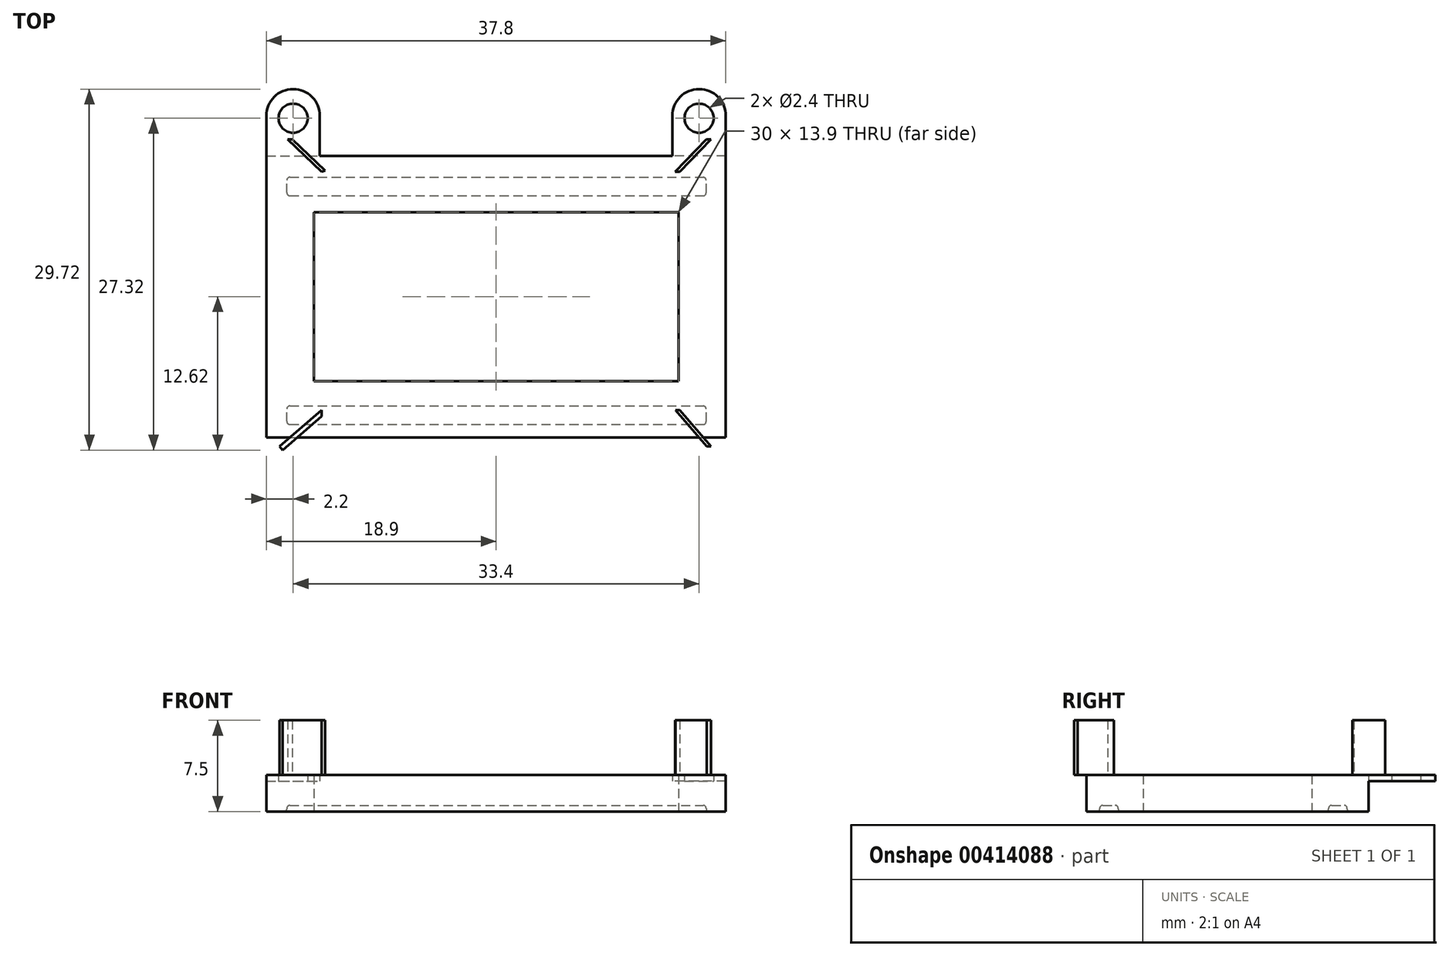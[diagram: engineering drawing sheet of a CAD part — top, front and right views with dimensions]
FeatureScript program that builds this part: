
annotation { "Feature Type Name" : "Feature", "Feature Type Description" : "" }
export const myFeature = defineFeature(function(context is Context, id is Id, definition is map)
    precondition{}
    {
        {
            var Q0;
            Q0=qCreatedBy(makeId("Top.planeOp"),FACE);
            var sketch = newSketch(context, id + "F0", { "sketchPlane" : qUnion([Q0])});
            skLineSegment(sketch, "E0.bottom", {"start": v(0, 0) * mm, "end": v(37.8, 0) * mm});
            skLineSegment(sketch, "E0.top", {"start": v(0, 23.2) * mm, "end": v(37.8, 23.2) * mm});
            skLineSegment(sketch, "E0.left", {"start": v(0, 0) * mm, "end": v(0, 23.2) * mm});
            skLineSegment(sketch, "E0.right", {"start": v(37.8, 0) * mm, "end": v(37.8, 23.2) * mm});
            skSolve(sketch);
        }
        {
            var Q0;
            Q0=makeQuery(id+"F0.imprint","IMPRINT",FACE,{"disambiguationData":[TD([[makeQuery(id+"F0.imprint","IMPRINT",EDGE,{"derivedFrom":sQuery(id+"F0.wireOp",EDGE,"E0.bottom")}),1.0]])]});
            extrude(context, id + "F1", {"entities" : qUnion([Q0]), "depth" : 3 * mm});
        }
        {
            var Q0;
            Q0=makeQuery(id+"F1.opExtrude","CAP_FACE",FACE,{"disambiguationData":[OSD([sQuery(id+"F0.wireOp",EDGE,"E0.bottom"),sQuery(id+"F0.wireOp",EDGE,"E0.top"),sQuery(id+"F0.wireOp",EDGE,"E0.left"),sQuery(id+"F0.wireOp",EDGE,"E0.right")])],"isStart":false});
            var sketch = newSketch(context, id + "F2", { "sketchPlane" : qUnion([Q0])});
            skLineSegment(sketch, "E1", {"start": v(4.54, 2.26) * mm, "end": v(1.07, -0.72) * mm});
            skLineSegment(sketch, "E2", {"start": v(1.07, -0.72) * mm, "end": v(1.32, -1.02) * mm});
            skLineSegment(sketch, "E3", {"start": v(1.32, -1.02) * mm, "end": v(4.54, 1.75) * mm});
            skLineSegment(sketch, "E4", {"start": v(4.54, 1.75) * mm, "end": v(4.54, 2.26) * mm});
            skLineSegment(sketch, "E5", {"start": v(34, 2.26) * mm, "end": v(36.57, -0.72) * mm});
            skLineSegment(sketch, "E6", {"start": v(36.57, -0.72) * mm, "end": v(36.23, -0.72) * mm});
            skLineSegment(sketch, "E7", {"start": v(36.23, -0.72) * mm, "end": v(33.66, 2.26) * mm});
            skLineSegment(sketch, "E8", {"start": v(33.66, 2.26) * mm, "end": v(34, 2.26) * mm});
            skLineSegment(sketch, "E9", {"start": v(34, 21.88) * mm, "end": v(36.57, 24.56) * mm});
            skLineSegment(sketch, "E10", {"start": v(36.57, 24.56) * mm, "end": v(36.21, 24.56) * mm});
            skLineSegment(sketch, "E11", {"start": v(36.21, 24.56) * mm, "end": v(33.64, 21.88) * mm});
            skLineSegment(sketch, "E12", {"start": v(33.64, 21.88) * mm, "end": v(34, 21.88) * mm});
            skLineSegment(sketch, "E13", {"start": v(4.54, 21.88) * mm, "end": v(1.75, 24.56) * mm});
            skLineSegment(sketch, "E14", {"start": v(1.75, 24.56) * mm, "end": v(2.13, 24.56) * mm});
            skLineSegment(sketch, "E15", {"start": v(2.13, 24.56) * mm, "end": v(4.82, 21.98) * mm});
            skLineSegment(sketch, "E16", {"start": v(4.82, 21.98) * mm, "end": v(4.54, 21.88) * mm});
            skSolve(sketch);
        }
        {
            var Q0;
            {var subQ0=sQuery(id+"F2.wireOp",EDGE,"E14");Q0=makeQuery(id+"F2.imprint","IMPRINT",FACE,{"disambiguationData":[TD([[makeQuery(id+"F2.imprint","IMPRINT",EDGE,{"derivedFrom":subQ0}),-1.0]])]});}
            var Q1;
            {var subQ0=sQuery(id+"F2.wireOp",EDGE,"E16");Q1=makeQuery(id+"F2.imprint","IMPRINT",FACE,{"disambiguationData":[TD([[makeQuery(id+"F2.imprint","IMPRINT",EDGE,{"derivedFrom":subQ0}),-1.0]])]});}
            var Q2;
            {var subQ0=sQuery(id+"F2.wireOp",EDGE,"E2");Q2=makeQuery(id+"F2.imprint","IMPRINT",FACE,{"disambiguationData":[TD([[makeQuery(id+"F2.imprint","IMPRINT",EDGE,{"derivedFrom":subQ0}),1.0]])]});}
            var Q3;
            {var subQ0=sQuery(id+"F2.wireOp",EDGE,"E4");Q3=makeQuery(id+"F2.imprint","IMPRINT",FACE,{"disambiguationData":[TD([[makeQuery(id+"F2.imprint","IMPRINT",EDGE,{"derivedFrom":subQ0}),1.0]])]});}
            var Q4;
            {var subQ0=sQuery(id+"F2.wireOp",EDGE,"E8");Q4=makeQuery(id+"F2.imprint","IMPRINT",FACE,{"disambiguationData":[TD([[makeQuery(id+"F2.imprint","IMPRINT",EDGE,{"derivedFrom":subQ0}),-1.0]])]});}
            var Q5;
            {var subQ0=sQuery(id+"F2.wireOp",EDGE,"E6");Q5=makeQuery(id+"F2.imprint","IMPRINT",FACE,{"disambiguationData":[TD([[makeQuery(id+"F2.imprint","IMPRINT",EDGE,{"derivedFrom":subQ0}),-1.0]])]});}
            var Q6;
            {var subQ0=sQuery(id+"F2.wireOp",EDGE,"E10");Q6=makeQuery(id+"F2.imprint","IMPRINT",FACE,{"disambiguationData":[TD([[makeQuery(id+"F2.imprint","IMPRINT",EDGE,{"derivedFrom":subQ0}),1.0]])]});}
            var Q7;
            {var subQ0=sQuery(id+"F2.wireOp",EDGE,"E12");Q7=makeQuery(id+"F2.imprint","IMPRINT",FACE,{"disambiguationData":[TD([[makeQuery(id+"F2.imprint","IMPRINT",EDGE,{"derivedFrom":subQ0}),1.0]])]});}
            extrude(context, id + "F3", {"entities" : qUnion([Q0, Q1, Q2, Q3, Q4, Q5, Q6, Q7]), "operationType" : NewBodyOperationType.ADD, "depth" : 4.5 * mm});
        }
        {
            var Q0;
            Q0=makeQuery(id+"F1.opExtrude","CAP_FACE",FACE,{"disambiguationData":[OSD([sQuery(id+"F0.wireOp",EDGE,"E0.bottom"),sQuery(id+"F0.wireOp",EDGE,"E0.top"),sQuery(id+"F0.wireOp",EDGE,"E0.left"),sQuery(id+"F0.wireOp",EDGE,"E0.right")])],"isStart":true});
            var sketch = newSketch(context, id + "F4", { "sketchPlane" : qUnion([Q0])});
            skLineSegment(sketch, "E17.bottom", {"start": v(33.9, -4.65) * mm, "end": v(3.9, -4.65) * mm});
            skLineSegment(sketch, "E17.top", {"start": v(33.9, -18.55) * mm, "end": v(3.9, -18.55) * mm});
            skLineSegment(sketch, "E17.left", {"start": v(33.9, -4.65) * mm, "end": v(33.9, -18.55) * mm});
            skLineSegment(sketch, "E17.right", {"start": v(3.9, -4.65) * mm, "end": v(3.9, -18.55) * mm});
            skPoint(sketch, "E17.middle", {"position": v(18.9, -11.6) * mm});
            skPoint(sketch, "E18.trimOffspring.end.orphan", {"position": v(37.8, -23.2) * mm});
            skPoint(sketch, "E19.start.orphan", {"position": v(0, 0) * mm});
            skLineSegment(sketch, "E20.bottom", {"start": v(1.68, -1.08) * mm, "end": v(36.18, -1.08) * mm});
            skLineSegment(sketch, "E20.top", {"start": v(1.68, -2.6) * mm, "end": v(36.18, -2.6) * mm});
            skLineSegment(sketch, "E20.left", {"start": v(1.68, -1.08) * mm, "end": v(1.68, -2.6) * mm});
            skLineSegment(sketch, "E20.right", {"start": v(36.18, -1.08) * mm, "end": v(36.18, -2.6) * mm});
            skLineSegment(sketch, "E21.bottom", {"start": v(1.68, -19.91) * mm, "end": v(36.18, -19.91) * mm});
            skLineSegment(sketch, "E21.top", {"start": v(1.68, -21.44) * mm, "end": v(36.18, -21.44) * mm});
            skLineSegment(sketch, "E21.left", {"start": v(1.68, -19.91) * mm, "end": v(1.68, -21.44) * mm});
            skLineSegment(sketch, "E21.right", {"start": v(36.18, -19.91) * mm, "end": v(36.18, -21.44) * mm});
            skSolve(sketch);
        }
        {
            var Q0;
            Q0=makeQuery(id+"F4.imprint","IMPRINT",FACE,{"disambiguationData":[TD([[makeQuery(id+"F4.imprint","IMPRINT",EDGE,{"derivedFrom":sQuery(id+"F4.wireOp",EDGE,"E17.bottom")}),1.0]])]});
            extrude(context, id + "F5", {"entities" : qUnion([Q0]), "operationType" : NewBodyOperationType.REMOVE, "oppositeDirection" : true, "depth" : 25.4 * mm});
        }
        {
            var Q0;
            Q0 = qSketchRegion(id + "F4", true);
            extrude(context, id + "F6", {"entities" : qUnion([Q0]), "operationType" : NewBodyOperationType.REMOVE, "oppositeDirection" : true, "depth" : .5 * mm});
        }
        {
            var Q0;
            Q0=makeQuery(id+"F6.boolean.opBoolean","COPY",EDGE,{"derivedFrom":makeQuery(id+"F6.opExtrude","CAP_EDGE",EDGE,{"disambiguationData":[OSD([sQuery(id+"F4.wireOp",EDGE,"E20.top")])],"isStart":false})});
            var Q1;
            Q1=makeQuery(id+"F6.boolean.opBoolean","COPY",EDGE,{"derivedFrom":makeQuery(id+"F6.opExtrude","CAP_EDGE",EDGE,{"disambiguationData":[OSD([sQuery(id+"F4.wireOp",EDGE,"E20.bottom")])],"isStart":false})});
            var Q2;
            Q2=makeQuery(id+"F6.boolean.opBoolean","COPY",EDGE,{"derivedFrom":makeQuery(id+"F6.opExtrude","CAP_EDGE",EDGE,{"disambiguationData":[OSD([sQuery(id+"F4.wireOp",EDGE,"E21.bottom")])],"isStart":false})});
            var Q3;
            Q3=makeQuery(id+"F6.boolean.opBoolean","COPY",EDGE,{"derivedFrom":makeQuery(id+"F6.opExtrude","CAP_EDGE",EDGE,{"disambiguationData":[OSD([sQuery(id+"F4.wireOp",EDGE,"E21.top")])],"isStart":false})});
            var Q4;
            Q4=makeQuery(id+"F6.boolean.opBoolean","COPY",EDGE,{"derivedFrom":makeQuery(id+"F6.opExtrude","SWEPT_EDGE",EDGE,{"disambiguationData":[OSD([sQuery(id+"F4.wireOp",EDGE,"E21.bottom"),sQuery(id+"F4.wireOp",EDGE,"E21.left")])]})});
            var Q5;
            Q5=makeQuery(id+"F6.boolean.opBoolean","COPY",EDGE,{"derivedFrom":makeQuery(id+"F6.opExtrude","SWEPT_EDGE",EDGE,{"disambiguationData":[OSD([sQuery(id+"F4.wireOp",EDGE,"E21.top"),sQuery(id+"F4.wireOp",EDGE,"E21.left")])]})});
            var Q6;
            Q6=makeQuery(id+"F6.boolean.opBoolean","COPY",EDGE,{"derivedFrom":makeQuery(id+"F6.opExtrude","SWEPT_EDGE",EDGE,{"disambiguationData":[OSD([sQuery(id+"F4.wireOp",EDGE,"E20.top"),sQuery(id+"F4.wireOp",EDGE,"E20.left")])]})});
            var Q7;
            Q7=makeQuery(id+"F6.boolean.opBoolean","COPY",EDGE,{"derivedFrom":makeQuery(id+"F6.opExtrude","SWEPT_EDGE",EDGE,{"disambiguationData":[OSD([sQuery(id+"F4.wireOp",EDGE,"E20.bottom"),sQuery(id+"F4.wireOp",EDGE,"E20.left")])]})});
            var Q8;
            Q8=makeQuery(id+"F6.boolean.opBoolean","COPY",EDGE,{"derivedFrom":makeQuery(id+"F6.opExtrude","CAP_EDGE",EDGE,{"disambiguationData":[OSD([sQuery(id+"F4.wireOp",EDGE,"E20.left")])],"isStart":false})});
            var Q9;
            Q9=makeQuery(id+"F6.boolean.opBoolean","COPY",EDGE,{"derivedFrom":makeQuery(id+"F6.opExtrude","CAP_EDGE",EDGE,{"disambiguationData":[OSD([sQuery(id+"F4.wireOp",EDGE,"E21.left")])],"isStart":false})});
            var Q10;
            Q10=makeQuery(id+"F6.boolean.opBoolean","COPY",EDGE,{"derivedFrom":makeQuery(id+"F6.opExtrude","SWEPT_EDGE",EDGE,{"disambiguationData":[OSD([sQuery(id+"F4.wireOp",EDGE,"E21.bottom"),sQuery(id+"F4.wireOp",EDGE,"E21.right")])]})});
            var Q11;
            Q11=makeQuery(id+"F6.boolean.opBoolean","COPY",EDGE,{"derivedFrom":makeQuery(id+"F6.opExtrude","SWEPT_EDGE",EDGE,{"disambiguationData":[OSD([sQuery(id+"F4.wireOp",EDGE,"E21.top"),sQuery(id+"F4.wireOp",EDGE,"E21.right")])]})});
            var Q12;
            Q12=makeQuery(id+"F6.boolean.opBoolean","COPY",EDGE,{"derivedFrom":makeQuery(id+"F6.opExtrude","CAP_EDGE",EDGE,{"disambiguationData":[OSD([sQuery(id+"F4.wireOp",EDGE,"E21.right")])],"isStart":false})});
            var Q13;
            Q13=makeQuery(id+"F6.boolean.opBoolean","COPY",EDGE,{"derivedFrom":makeQuery(id+"F6.opExtrude","SWEPT_EDGE",EDGE,{"disambiguationData":[OSD([sQuery(id+"F4.wireOp",EDGE,"E20.bottom"),sQuery(id+"F4.wireOp",EDGE,"E20.right")])]})});
            var Q14;
            Q14=makeQuery(id+"F6.boolean.opBoolean","COPY",EDGE,{"derivedFrom":makeQuery(id+"F6.opExtrude","SWEPT_EDGE",EDGE,{"disambiguationData":[OSD([sQuery(id+"F4.wireOp",EDGE,"E20.top"),sQuery(id+"F4.wireOp",EDGE,"E20.right")])]})});
            var Q15;
            Q15=makeQuery(id+"F6.boolean.opBoolean","COPY",EDGE,{"derivedFrom":makeQuery(id+"F6.opExtrude","CAP_EDGE",EDGE,{"disambiguationData":[OSD([sQuery(id+"F4.wireOp",EDGE,"E20.right")])],"isStart":false})});
            fillet(context, id + "F7", {"entities" : qUnion([Q0, Q1, Q2, Q3, Q4, Q5, Q6, Q7, Q8, Q9, Q10, Q11, Q12, Q13, Q14, Q15]), "radius" : .25 * mm, "tangentPropagation" : true, "allowEdgeOverflow" : false});
        }
        {
            var Q0;
            Q0=makeQuery(id+"F6.boolean.opBoolean","COPY",EDGE,{"derivedFrom":makeQuery(id+"F6.opExtrude","CAP_EDGE",EDGE,{"disambiguationData":[OSD([sQuery(id+"F4.wireOp",EDGE,"E20.bottom")])],"isStart":true})});
            var Q1;
            Q1=makeQuery(id+"F6.boolean.opBoolean","COPY",EDGE,{"derivedFrom":makeQuery(id+"F6.opExtrude","CAP_EDGE",EDGE,{"disambiguationData":[OSD([sQuery(id+"F4.wireOp",EDGE,"E20.right")])],"isStart":true})});
            var Q2;
            Q2=makeQuery(id+"F7.opFillet","BLEND_EDGE",EDGE,{"blendedFrom":[makeQuery(id+"F6.boolean.opBoolean","COPY",EDGE,{"derivedFrom":makeQuery(id+"F6.opExtrude","SWEPT_EDGE",EDGE,{"disambiguationData":[OSD([sQuery(id+"F4.wireOp",EDGE,"E20.bottom"),sQuery(id+"F4.wireOp",EDGE,"E20.right")])]})}),makeQuery(id+"F1.opExtrude","CAP_FACE",FACE,{"disambiguationData":[OSD([sQuery(id+"F0.wireOp",EDGE,"E0.bottom"),sQuery(id+"F0.wireOp",EDGE,"E0.top"),sQuery(id+"F0.wireOp",EDGE,"E0.left"),sQuery(id+"F0.wireOp",EDGE,"E0.right")])],"isStart":true})],"blendedInto":[makeQuery(id+"F1.opExtrude","CAP_FACE",FACE,{"disambiguationData":[OSD([sQuery(id+"F0.wireOp",EDGE,"E0.bottom"),sQuery(id+"F0.wireOp",EDGE,"E0.top"),sQuery(id+"F0.wireOp",EDGE,"E0.left"),sQuery(id+"F0.wireOp",EDGE,"E0.right")])],"isStart":true})]});
            var Q3;
            Q3=makeQuery(id+"F7.opFillet","BLEND_EDGE",EDGE,{"blendedFrom":[makeQuery(id+"F6.boolean.opBoolean","COPY",EDGE,{"derivedFrom":makeQuery(id+"F6.opExtrude","SWEPT_EDGE",EDGE,{"disambiguationData":[OSD([sQuery(id+"F4.wireOp",EDGE,"E20.top"),sQuery(id+"F4.wireOp",EDGE,"E20.right")])]})}),makeQuery(id+"F1.opExtrude","CAP_FACE",FACE,{"disambiguationData":[OSD([sQuery(id+"F0.wireOp",EDGE,"E0.bottom"),sQuery(id+"F0.wireOp",EDGE,"E0.top"),sQuery(id+"F0.wireOp",EDGE,"E0.left"),sQuery(id+"F0.wireOp",EDGE,"E0.right")])],"isStart":true})],"blendedInto":[makeQuery(id+"F1.opExtrude","CAP_FACE",FACE,{"disambiguationData":[OSD([sQuery(id+"F0.wireOp",EDGE,"E0.bottom"),sQuery(id+"F0.wireOp",EDGE,"E0.top"),sQuery(id+"F0.wireOp",EDGE,"E0.left"),sQuery(id+"F0.wireOp",EDGE,"E0.right")])],"isStart":true})]});
            var Q4;
            Q4=makeQuery(id+"F6.boolean.opBoolean","COPY",EDGE,{"derivedFrom":makeQuery(id+"F6.opExtrude","CAP_EDGE",EDGE,{"disambiguationData":[OSD([sQuery(id+"F4.wireOp",EDGE,"E20.left")])],"isStart":true})});
            var Q5;
            Q5=makeQuery(id+"F7.opFillet","BLEND_EDGE",EDGE,{"blendedFrom":[makeQuery(id+"F6.boolean.opBoolean","COPY",EDGE,{"derivedFrom":makeQuery(id+"F6.opExtrude","SWEPT_EDGE",EDGE,{"disambiguationData":[OSD([sQuery(id+"F4.wireOp",EDGE,"E20.bottom"),sQuery(id+"F4.wireOp",EDGE,"E20.left")])]})}),makeQuery(id+"F1.opExtrude","CAP_FACE",FACE,{"disambiguationData":[OSD([sQuery(id+"F0.wireOp",EDGE,"E0.bottom"),sQuery(id+"F0.wireOp",EDGE,"E0.top"),sQuery(id+"F0.wireOp",EDGE,"E0.left"),sQuery(id+"F0.wireOp",EDGE,"E0.right")])],"isStart":true})],"blendedInto":[makeQuery(id+"F1.opExtrude","CAP_FACE",FACE,{"disambiguationData":[OSD([sQuery(id+"F0.wireOp",EDGE,"E0.bottom"),sQuery(id+"F0.wireOp",EDGE,"E0.top"),sQuery(id+"F0.wireOp",EDGE,"E0.left"),sQuery(id+"F0.wireOp",EDGE,"E0.right")])],"isStart":true})]});
            var Q6;
            Q6=makeQuery(id+"F7.opFillet","BLEND_EDGE",EDGE,{"blendedFrom":[makeQuery(id+"F6.boolean.opBoolean","COPY",EDGE,{"derivedFrom":makeQuery(id+"F6.opExtrude","SWEPT_EDGE",EDGE,{"disambiguationData":[OSD([sQuery(id+"F4.wireOp",EDGE,"E20.top"),sQuery(id+"F4.wireOp",EDGE,"E20.left")])]})}),makeQuery(id+"F1.opExtrude","CAP_FACE",FACE,{"disambiguationData":[OSD([sQuery(id+"F0.wireOp",EDGE,"E0.bottom"),sQuery(id+"F0.wireOp",EDGE,"E0.top"),sQuery(id+"F0.wireOp",EDGE,"E0.left"),sQuery(id+"F0.wireOp",EDGE,"E0.right")])],"isStart":true})],"blendedInto":[makeQuery(id+"F1.opExtrude","CAP_FACE",FACE,{"disambiguationData":[OSD([sQuery(id+"F0.wireOp",EDGE,"E0.bottom"),sQuery(id+"F0.wireOp",EDGE,"E0.top"),sQuery(id+"F0.wireOp",EDGE,"E0.left"),sQuery(id+"F0.wireOp",EDGE,"E0.right")])],"isStart":true})]});
            var Q7;
            Q7=makeQuery(id+"F6.boolean.opBoolean","COPY",EDGE,{"derivedFrom":makeQuery(id+"F6.opExtrude","CAP_EDGE",EDGE,{"disambiguationData":[OSD([sQuery(id+"F4.wireOp",EDGE,"E20.top")])],"isStart":true})});
            fillet(context, id + "F8", {"entities" : qUnion([Q0, Q1, Q2, Q3, Q4, Q5, Q6, Q7]), "radius" : .2 * mm, "tangentPropagation" : true, "allowEdgeOverflow" : false});
        }
        {
            var Q0;
            Q0=makeQuery(id+"F6.boolean.opBoolean","COPY",EDGE,{"derivedFrom":makeQuery(id+"F6.opExtrude","CAP_EDGE",EDGE,{"disambiguationData":[OSD([sQuery(id+"F4.wireOp",EDGE,"E21.bottom")])],"isStart":true})});
            var Q1;
            Q1=makeQuery(id+"F7.opFillet","BLEND_EDGE",EDGE,{"blendedFrom":[makeQuery(id+"F6.boolean.opBoolean","COPY",EDGE,{"derivedFrom":makeQuery(id+"F6.opExtrude","SWEPT_EDGE",EDGE,{"disambiguationData":[OSD([sQuery(id+"F4.wireOp",EDGE,"E21.bottom"),sQuery(id+"F4.wireOp",EDGE,"E21.right")])]})}),makeQuery(id+"F1.opExtrude","CAP_FACE",FACE,{"disambiguationData":[OSD([sQuery(id+"F0.wireOp",EDGE,"E0.bottom"),sQuery(id+"F0.wireOp",EDGE,"E0.top"),sQuery(id+"F0.wireOp",EDGE,"E0.left"),sQuery(id+"F0.wireOp",EDGE,"E0.right")])],"isStart":true})],"blendedInto":[makeQuery(id+"F1.opExtrude","CAP_FACE",FACE,{"disambiguationData":[OSD([sQuery(id+"F0.wireOp",EDGE,"E0.bottom"),sQuery(id+"F0.wireOp",EDGE,"E0.top"),sQuery(id+"F0.wireOp",EDGE,"E0.left"),sQuery(id+"F0.wireOp",EDGE,"E0.right")])],"isStart":true})]});
            var Q2;
            Q2=makeQuery(id+"F6.boolean.opBoolean","COPY",EDGE,{"derivedFrom":makeQuery(id+"F6.opExtrude","CAP_EDGE",EDGE,{"disambiguationData":[OSD([sQuery(id+"F4.wireOp",EDGE,"E21.right")])],"isStart":true})});
            var Q3;
            Q3=makeQuery(id+"F7.opFillet","BLEND_EDGE",EDGE,{"blendedFrom":[makeQuery(id+"F6.boolean.opBoolean","COPY",EDGE,{"derivedFrom":makeQuery(id+"F6.opExtrude","SWEPT_EDGE",EDGE,{"disambiguationData":[OSD([sQuery(id+"F4.wireOp",EDGE,"E21.top"),sQuery(id+"F4.wireOp",EDGE,"E21.right")])]})}),makeQuery(id+"F1.opExtrude","CAP_FACE",FACE,{"disambiguationData":[OSD([sQuery(id+"F0.wireOp",EDGE,"E0.bottom"),sQuery(id+"F0.wireOp",EDGE,"E0.top"),sQuery(id+"F0.wireOp",EDGE,"E0.left"),sQuery(id+"F0.wireOp",EDGE,"E0.right")])],"isStart":true})],"blendedInto":[makeQuery(id+"F1.opExtrude","CAP_FACE",FACE,{"disambiguationData":[OSD([sQuery(id+"F0.wireOp",EDGE,"E0.bottom"),sQuery(id+"F0.wireOp",EDGE,"E0.top"),sQuery(id+"F0.wireOp",EDGE,"E0.left"),sQuery(id+"F0.wireOp",EDGE,"E0.right")])],"isStart":true})]});
            var Q4;
            Q4=makeQuery(id+"F6.boolean.opBoolean","COPY",EDGE,{"derivedFrom":makeQuery(id+"F6.opExtrude","CAP_EDGE",EDGE,{"disambiguationData":[OSD([sQuery(id+"F4.wireOp",EDGE,"E21.top")])],"isStart":true})});
            var Q5;
            Q5=makeQuery(id+"F7.opFillet","BLEND_EDGE",EDGE,{"blendedFrom":[makeQuery(id+"F6.boolean.opBoolean","COPY",EDGE,{"derivedFrom":makeQuery(id+"F6.opExtrude","SWEPT_EDGE",EDGE,{"disambiguationData":[OSD([sQuery(id+"F4.wireOp",EDGE,"E21.top"),sQuery(id+"F4.wireOp",EDGE,"E21.left")])]})}),makeQuery(id+"F1.opExtrude","CAP_FACE",FACE,{"disambiguationData":[OSD([sQuery(id+"F0.wireOp",EDGE,"E0.bottom"),sQuery(id+"F0.wireOp",EDGE,"E0.top"),sQuery(id+"F0.wireOp",EDGE,"E0.left"),sQuery(id+"F0.wireOp",EDGE,"E0.right")])],"isStart":true})],"blendedInto":[makeQuery(id+"F1.opExtrude","CAP_FACE",FACE,{"disambiguationData":[OSD([sQuery(id+"F0.wireOp",EDGE,"E0.bottom"),sQuery(id+"F0.wireOp",EDGE,"E0.top"),sQuery(id+"F0.wireOp",EDGE,"E0.left"),sQuery(id+"F0.wireOp",EDGE,"E0.right")])],"isStart":true})]});
            var Q6;
            Q6=makeQuery(id+"F6.boolean.opBoolean","COPY",EDGE,{"derivedFrom":makeQuery(id+"F6.opExtrude","CAP_EDGE",EDGE,{"disambiguationData":[OSD([sQuery(id+"F4.wireOp",EDGE,"E21.left")])],"isStart":true})});
            var Q7;
            Q7=makeQuery(id+"F7.opFillet","BLEND_EDGE",EDGE,{"blendedFrom":[makeQuery(id+"F6.boolean.opBoolean","COPY",EDGE,{"derivedFrom":makeQuery(id+"F6.opExtrude","SWEPT_EDGE",EDGE,{"disambiguationData":[OSD([sQuery(id+"F4.wireOp",EDGE,"E21.bottom"),sQuery(id+"F4.wireOp",EDGE,"E21.left")])]})}),makeQuery(id+"F1.opExtrude","CAP_FACE",FACE,{"disambiguationData":[OSD([sQuery(id+"F0.wireOp",EDGE,"E0.bottom"),sQuery(id+"F0.wireOp",EDGE,"E0.top"),sQuery(id+"F0.wireOp",EDGE,"E0.left"),sQuery(id+"F0.wireOp",EDGE,"E0.right")])],"isStart":true})],"blendedInto":[makeQuery(id+"F1.opExtrude","CAP_FACE",FACE,{"disambiguationData":[OSD([sQuery(id+"F0.wireOp",EDGE,"E0.bottom"),sQuery(id+"F0.wireOp",EDGE,"E0.top"),sQuery(id+"F0.wireOp",EDGE,"E0.left"),sQuery(id+"F0.wireOp",EDGE,"E0.right")])],"isStart":true})]});
            fillet(context, id + "F9", {"entities" : qUnion([Q0, Q1, Q2, Q3, Q4, Q5, Q6, Q7]), "radius" : .2 * mm, "tangentPropagation" : true, "allowEdgeOverflow" : false});
        }
        {
            var Q0;
            Q0=makeQuery(id+"F1.opExtrude","SWEPT_FACE",FACE,{"disambiguationData":[OSD([sQuery(id+"F0.wireOp",EDGE,"E0.top")])]});
            var sketch = newSketch(context, id + "F10", { "sketchPlane" : qUnion([Q0])});
            skLineSegment(sketch, "E22.bottom", {"start": v(0, 3) * mm, "end": v(-4.4, 3) * mm});
            skLineSegment(sketch, "E22.top", {"start": v(0, 2.5) * mm, "end": v(-4.4, 2.5) * mm});
            skLineSegment(sketch, "E22.left", {"start": v(0, 3) * mm, "end": v(0, 2.5) * mm});
            skLineSegment(sketch, "E22.right", {"start": v(-4.4, 3) * mm, "end": v(-4.4, 2.5) * mm});
            skLineSegment(sketch, "E23.bottom", {"start": v(-37.8, 3) * mm, "end": v(-33.4, 3) * mm});
            skLineSegment(sketch, "E23.top", {"start": v(-37.8, 2.5) * mm, "end": v(-33.4, 2.5) * mm});
            skLineSegment(sketch, "E23.left", {"start": v(-37.8, 3) * mm, "end": v(-37.8, 2.5) * mm});
            skLineSegment(sketch, "E23.right", {"start": v(-33.4, 3) * mm, "end": v(-33.4, 2.5) * mm});
            skSolve(sketch);
        }
        {
            var Q0;
            Q0=makeQuery(id+"F10.imprint","IMPRINT",FACE,{"disambiguationData":[TD([[makeQuery(id+"F10.imprint","IMPRINT",EDGE,{"derivedFrom":sQuery(id+"F10.wireOp",EDGE,"E23.top")}),1.0]])]});
            var Q1;
            Q1=makeQuery(id+"F10.imprint","IMPRINT",FACE,{"disambiguationData":[TD([[makeQuery(id+"F10.imprint","IMPRINT",EDGE,{"derivedFrom":sQuery(id+"F10.wireOp",EDGE,"E22.top")}),-1.0]])]});
            extrude(context, id + "F11", {"entities" : qUnion([Q0, Q1]), "operationType" : NewBodyOperationType.ADD, "depth" : 5.5 * mm});
        }
        {
            var Q0;
            Q0=makeQuery(id+"F11.opExtrude","CAP_EDGE",EDGE,{"disambiguationData":[OSD([sQuery(id+"F10.wireOp",EDGE,"E22.left")])],"isStart":false});
            var Q1;
            Q1=makeQuery(id+"F11.opExtrude","CAP_EDGE",EDGE,{"disambiguationData":[OSD([sQuery(id+"F10.wireOp",EDGE,"E22.right")])],"isStart":false});
            fillet(context, id + "F12", {"entities" : qUnion([Q0, Q1]), "radius" : 2.2 * mm, "tangentPropagation" : true, "allowEdgeOverflow" : false});
        }
        {
            var Q0;
            Q0=makeQuery(id+"F11.opExtrude","CAP_EDGE",EDGE,{"disambiguationData":[OSD([sQuery(id+"F10.wireOp",EDGE,"E23.right")])],"isStart":false});
            var Q1;
            Q1=makeQuery(id+"F11.opExtrude","CAP_EDGE",EDGE,{"disambiguationData":[OSD([sQuery(id+"F10.wireOp",EDGE,"E23.left")])],"isStart":false});
            fillet(context, id + "F13", {"entities" : qUnion([Q0, Q1]), "radius" : 2.2 * mm, "tangentPropagation" : true, "allowEdgeOverflow" : false});
        }
        {
            var Q0;
            Q0=makeQuery(id+"F11.opExtrude","SWEPT_FACE",FACE,{"disambiguationData":[OSD([sQuery(id+"F10.wireOp",EDGE,"E23.top")])]});
            var sketch = newSketch(context, id + "F14", { "sketchPlane" : qUnion([Q0])});
            skPoint(sketch, "E24.orphan", {"position": v(35.6, -22.68) * mm});
            skPoint(sketch, "E25.orphan", {"position": v(35.6, -23.2) * mm});
            skPoint(sketch, "E26.start.orphan", {"position": v(35.6, -26.5) * mm});
            skPoint(sketch, "E27.center.orphan", {"position": v(35.6, -24.6) * mm});
            skPoint(sketch, "E28.end.orphan", {"position": v(35.6, -25.95) * mm});
            skCircle(sketch, "E29", {"center": v(35.6, -26.3) * mm, "radius": 1.2 * mm});
            skPoint(sketch, "E30.orphan", {"position": v(35.6, -25.1) * mm});
            skPoint(sketch, "E31.end.orphan", {"position": v(35.6, -27.5) * mm});
            skPoint(sketch, "E31.start.orphan", {"position": v(35.6, -28.7) * mm});
            skSolve(sketch);
        }
        {
            var Q0;
            Q0=makeQuery(id+"F11.opExtrude","SWEPT_FACE",FACE,{"disambiguationData":[OSD([sQuery(id+"F10.wireOp",EDGE,"E22.top")])]});
            var sketch = newSketch(context, id + "F15", { "sketchPlane" : qUnion([Q0])});
            skPoint(sketch, "E32.orphan", {"position": v(2.2, -24.1) * mm});
            skPoint(sketch, "E33.start.orphan", {"position": v(2.2, -23.2) * mm});
            skPoint(sketch, "E34.end.orphan", {"position": v(2.35, -25.75) * mm});
            skPoint(sketch, "E35.center.orphan", {"position": v(2.28, -24.93) * mm});
            skCircle(sketch, "E36", {"center": v(2.2, -26.3) * mm, "radius": 1.2 * mm});
            skPoint(sketch, "E37.orphan", {"position": v(2.2, -25.1) * mm});
            skPoint(sketch, "E38.end.orphan", {"position": v(2.2, -27.5) * mm});
            skSolve(sketch);
        }
        {
            var Q0;
            Q0=makeQuery(id+"F15.imprint","IMPRINT",FACE,{"disambiguationData":[TD([[makeQuery(id+"F15.imprint","IMPRINT",EDGE,{"derivedFrom":sQuery(id+"F15.wireOp",EDGE,"E36")}),1.0]])]});
            var Q1;
            Q1=makeQuery(id+"F14.imprint","IMPRINT",FACE,{"disambiguationData":[TD([[makeQuery(id+"F14.imprint","IMPRINT",EDGE,{"derivedFrom":sQuery(id+"F14.wireOp",EDGE,"E29")}),1.0]])]});
            extrude(context, id + "F16", {"entities" : qUnion([Q0, Q1]), "operationType" : NewBodyOperationType.REMOVE, "oppositeDirection" : true, "depth" : 25.4 * mm});
        }
    });
